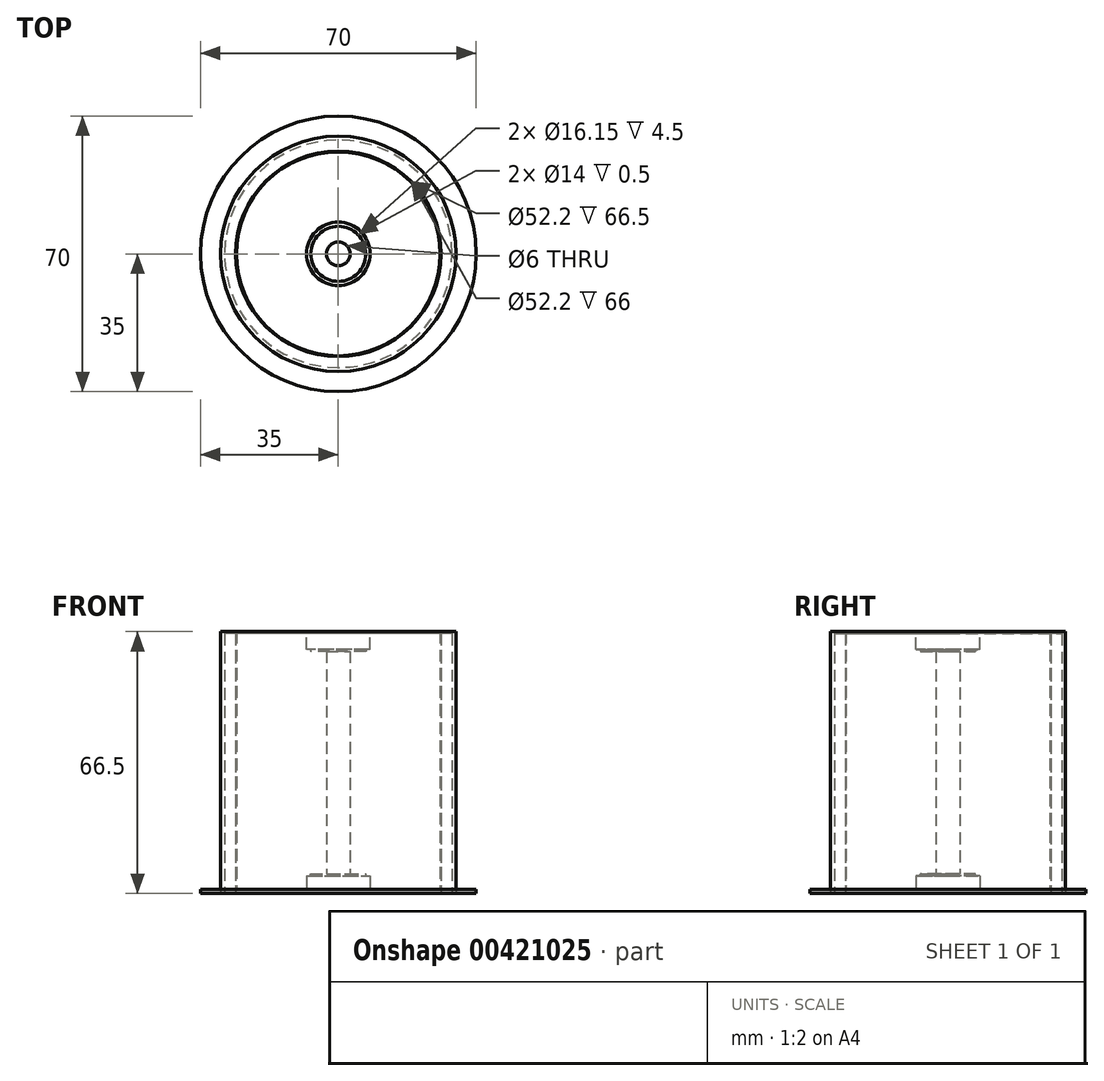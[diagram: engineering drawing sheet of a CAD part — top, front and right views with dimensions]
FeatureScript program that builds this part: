
annotation { "Feature Type Name" : "Feature", "Feature Type Description" : "" }
export const myFeature = defineFeature(function(context is Context, id is Id, definition is map)
    precondition{}
    {
        {
            var Q0;
            Q0=qCreatedBy(makeId("Top.planeOp"),FACE);
            var sketch = newSketch(context, id + "F0", { "sketchPlane" : qUnion([Q0])});
            skCircle(sketch, "E0", {"center": v(0, 0) * mm, "radius": 25.9 * mm});
            skCircle(sketch, "E1", {"center": v(0, 0) * mm, "radius": 3 * mm});
            skSolve(sketch);
        }
        {
            var Q0;
            Q0 = qSketchRegion(id + "F0", true);
            extrude(context, id + "F1", {"entities" : qUnion([Q0]), "depth" : 66.5 * mm});
        }
        {
            var Q0;
            Q0=makeQuery(id+"F1.opExtrude","CAP_FACE",FACE,{"disambiguationData":[OSD([sQuery(id+"F0.wireOp",EDGE,"E0"),sQuery(id+"F0.wireOp",EDGE,"E1")])],"isStart":true});
            var sketch = newSketch(context, id + "F2", { "sketchPlane" : qUnion([Q0])});
            skCircle(sketch, "E2.0", {"center": v(0, 0) * mm, "radius": 3 * mm});
            skCircle(sketch, "E3", {"center": v(0, 0) * mm, "radius": 35 * mm});
            skSolve(sketch);
        }
        {
            var Q0;
            Q0 = qSketchRegion(id + "F2", true);
            extrude(context, id + "F3", {"entities" : qUnion([Q0]), "operationType" : NewBodyOperationType.ADD, "oppositeDirection" : true, "depth" : 1 * mm});
        }
        {
            var Q0;
            Q0=makeQuery(id+"F1.opExtrude","CAP_FACE",FACE,{"disambiguationData":[OSD([sQuery(id+"F0.wireOp",EDGE,"E0"),sQuery(id+"F0.wireOp",EDGE,"E1")])],"isStart":false});
            var sketch = newSketch(context, id + "F4", { "sketchPlane" : qUnion([Q0])});
            skCircle(sketch, "E4", {"center": v(0, 0) * mm, "radius": 8.07 * mm});
            skSolve(sketch);
        }
        {
            var Q0;
            Q0 = qSketchRegion(id + "F4", true);
            extrude(context, id + "F5", {"entities" : qUnion([Q0]), "operationType" : NewBodyOperationType.REMOVE, "oppositeDirection" : true, "depth" : 5 * mm});
        }
        {
            var Q0;
            Q0=makeQuery(id+"F1.opExtrude","CAP_FACE",FACE,{"disambiguationData":[OSD([sQuery(id+"F0.wireOp",EDGE,"E0"),sQuery(id+"F0.wireOp",EDGE,"E1")])],"isStart":true});
            var sketch = newSketch(context, id + "F6", { "sketchPlane" : qUnion([Q0])});
            skCircle(sketch, "E5.0", {"center": v(0, 0) * mm, "radius": 8.07 * mm});
            skSolve(sketch);
        }
        {
            var Q0;
            Q0 = qSketchRegion(id + "F6", true);
            extrude(context, id + "F7", {"entities" : qUnion([Q0]), "operationType" : NewBodyOperationType.REMOVE, "oppositeDirection" : true, "depth" : 5 * mm});
        }
        {
            var Q0;
            Q0=makeQuery(id+"F5.boolean.opBoolean","COPY",FACE,{"derivedFrom":makeQuery(id+"F5.opExtrude","CAP_FACE",FACE,{"disambiguationData":[OSD([sQuery(id+"F4.wireOp",EDGE,"E4")])],"isStart":false})});
            var sketch = newSketch(context, id + "F8", { "sketchPlane" : qUnion([Q0])});
            skCircle(sketch, "E6", {"center": v(0, 0) * mm, "radius": 7 * mm});
            skCircle(sketch, "E7.0", {"center": v(0, 0) * mm, "radius": 8.07 * mm});
            skSolve(sketch);
        }
        {
            var Q0;
            Q0 = qSketchRegion(id + "F8", true);
            extrude(context, id + "F9", {"entities" : qUnion([Q0]), "operationType" : NewBodyOperationType.ADD, "depth" : 0.5 * mm});
        }
        {
            var Q0;
            Q0=makeQuery(id+"F7.boolean.opBoolean","COPY",FACE,{"derivedFrom":makeQuery(id+"F7.opExtrude","CAP_FACE",FACE,{"disambiguationData":[OSD([sQuery(id+"F6.wireOp",EDGE,"E5.0")])],"isStart":false})});
            var sketch = newSketch(context, id + "F10", { "sketchPlane" : qUnion([Q0])});
            skCircle(sketch, "E8.0", {"center": v(0, 0) * mm, "radius": 8.07 * mm});
            skCircle(sketch, "E9.0", {"center": v(0, 0) * mm, "radius": 7 * mm});
            skSolve(sketch);
        }
        {
            var Q0;
            Q0 = qSketchRegion(id + "F10", true);
            extrude(context, id + "F11", {"entities" : qUnion([Q0]), "operationType" : NewBodyOperationType.ADD, "depth" : 0.5 * mm});
        }
        {
            var Q0;
            Q0=qCreatedBy(makeId("Top.planeOp"),FACE);
            var sketch = newSketch(context, id + "F12", { "sketchPlane" : qUnion([Q0])});
            skCircle(sketch, "E10.0", {"center": v(0, 0) * mm, "radius": 26.1 * mm});
            skCircle(sketch, "E11", {"center": v(0, 0) * mm, "radius": 29.9 * mm});
            skSolve(sketch);
        }
        {
            var Q0;
            Q0 = qSketchRegion(id + "F12", true);
            extrude(context, id + "F13", {"entities" : qUnion([Q0]), "depth" : 66.5 * mm});
        }
        {
            var Q0;
            Q0=qCreatedBy(makeId("Top.planeOp"),FACE);
            var sketch = newSketch(context, id + "F14", { "sketchPlane" : qUnion([Q0])});
            skCircle(sketch, "E12.0", {"center": v(0, 0) * mm, "radius": 26.1 * mm});
            skCircle(sketch, "E13", {"center": v(0, 0) * mm, "radius": 28.9 * mm});
            skSolve(sketch);
        }
        {
            var Q0;
            Q0 = qSketchRegion(id + "F14", true);
            extrude(context, id + "F15", {"entities" : qUnion([Q0]), "depth" : 66 * mm});
        }
    });
